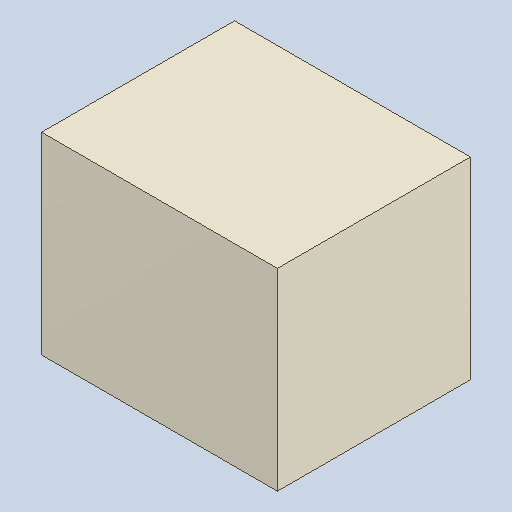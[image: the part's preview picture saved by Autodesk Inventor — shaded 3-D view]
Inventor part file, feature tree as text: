
AUTODESK INVENTOR PART (.ipt)
format: ipt  version: 2023.4 (Build 274418000, 418)  size: 81,920 bytes
history: native  units: mm
features: extrude x1
ambient origin geometry x8: Origin, YZ Plane, XZ Plane, XY Plane, X Axis, Y Axis, Z Axis, Center Point
bodies: Solid1 (feature_tree)
feature tree (1):
  extrude  "Extruded_9"  [1 undecoded]
note: 1 required parameter value undecoded (feature->parameter linkage not recoverable at this tier; creation-order binding heuristic only, values carry confidence <= 0.55)
